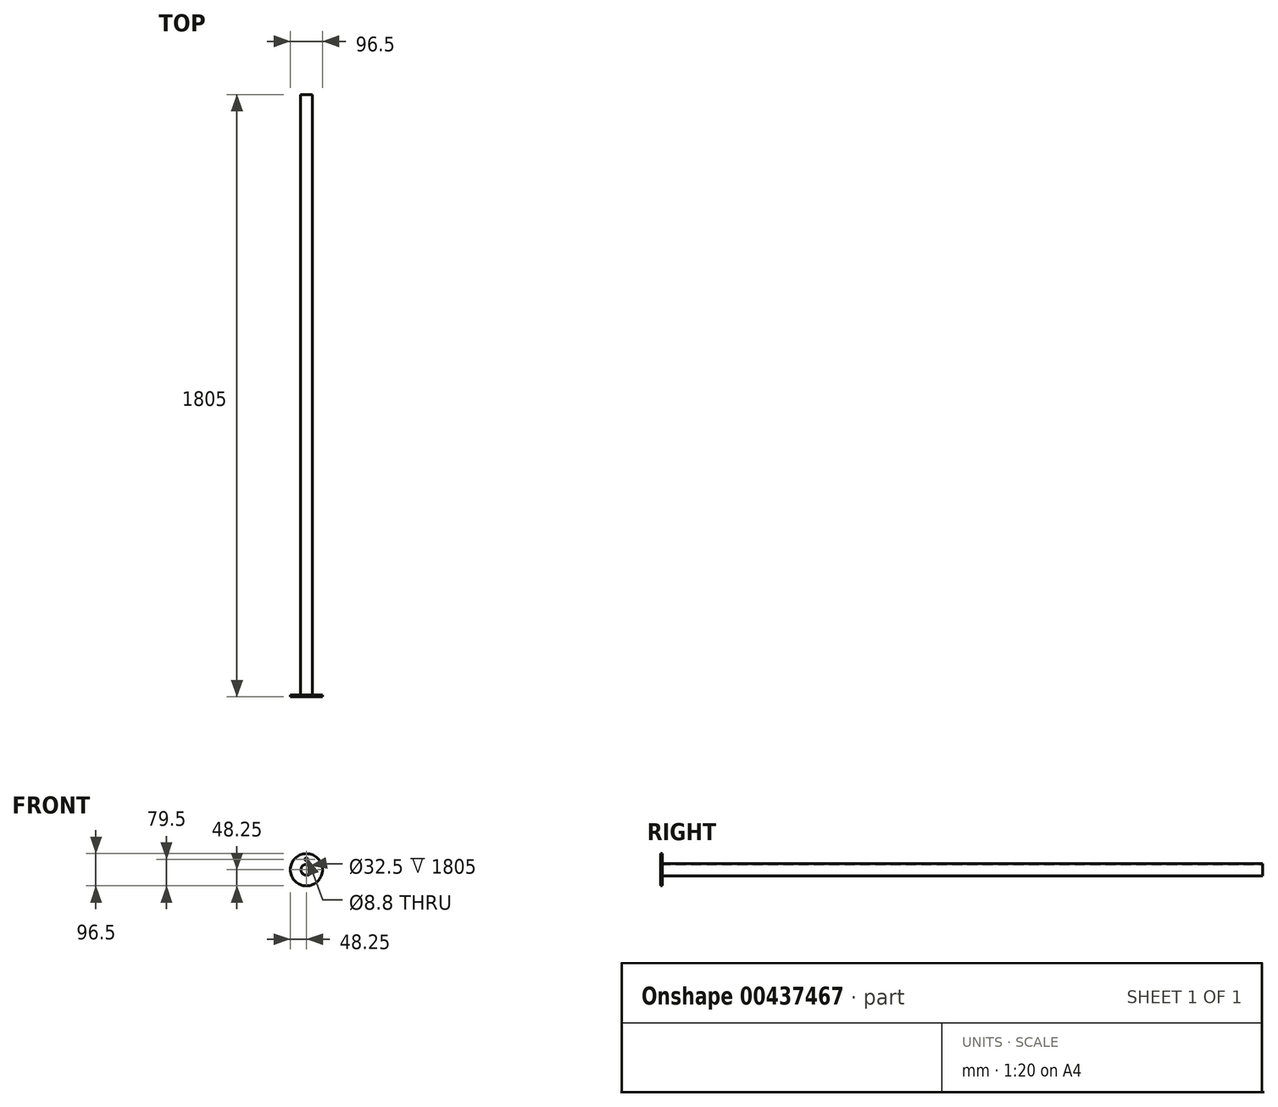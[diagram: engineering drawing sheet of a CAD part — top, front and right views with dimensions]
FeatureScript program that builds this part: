
annotation { "Feature Type Name" : "Feature", "Feature Type Description" : "" }
export const myFeature = defineFeature(function(context is Context, id is Id, definition is map)
    precondition{}
    {
        {
            var Q0;
            Q0=qCreatedBy(makeId("Front.planeOp"),FACE);
            var sketch = newSketch(context, id + "F0", { "sketchPlane" : qUnion([Q0])});
            skCircle(sketch, "E0", {"center": v(0, 0) * mm, "radius": 18.25 * mm});
            skCircle(sketch, "E1", {"center": v(0, 0) * mm, "radius": 16.25 * mm});
            skSolve(sketch);
        }
        {
            var Q0;
            Q0=makeQuery(id+"F0.imprint","IMPRINT",FACE,{"disambiguationData":[TD([[makeQuery(id+"F0.imprint","IMPRINT",EDGE,{"derivedFrom":sQuery(id+"F0.wireOp",EDGE,"E0")}),1.0]])]});
            extrude(context, id + "F1", {"entities" : qUnion([Q0]), "depth" : 1800 * mm});
        }
        {
            var Q0;
            Q0=makeQuery(id+"F1.opExtrude","CAP_FACE",FACE,{"disambiguationData":[OSD([sQuery(id+"F0.wireOp",EDGE,"E0"),sQuery(id+"F0.wireOp",EDGE,"E1")])],"isStart":false});
            var sketch = newSketch(context, id + "F2", { "sketchPlane" : qUnion([Q0])});
            skCircle(sketch, "E2", {"center": v(0, 0) * mm, "radius": 48.25 * mm});
            skSolve(sketch);
        }
        {
            var Q0;
            Q0=makeQuery(id+"F2.imprint","IMPRINT",FACE,{"disambiguationData":[TD([[makeQuery(id+"F2.imprint","IMPRINT",EDGE,{"derivedFrom":sQuery(id+"F2.wireOp",EDGE,"E2")}),1.0]])]});
            var Q1;
            Q1=makeQuery(id+"F2.imprint","IMPRINT",FACE,{"disambiguationData":[TD([[makeQuery(id+"F2.imprint","IMPRINT",EDGE,{"derivedFrom":makeQuery(id+"F1.opExtrude","CAP_EDGE",EDGE,{"disambiguationData":[OSD([sQuery(id+"F0.wireOp",EDGE,"E0")])],"isStart":false})}),1.0]])]});
            extrude(context, id + "F3", {"entities" : qUnion([Q0, Q1]), "operationType" : NewBodyOperationType.ADD, "depth" : 5 * mm});
        }
        {
            var Q0;
            Q0=makeQuery(id+"F3.opExtrude","CAP_FACE",FACE,{"disambiguationData":[OSD([sQuery(id+"F0.wireOp",EDGE,"E1"),sQuery(id+"F2.wireOp",EDGE,"E2")])],"isStart":false});
            var sketch = newSketch(context, id + "F4", { "sketchPlane" : qUnion([Q0])});
            skPoint(sketch, "E3", {"position": v(0, 31.25) * mm});
            skSolve(sketch);
        }
        {
            var Q0;
            Q0=sQuery(id+"F4.wireOp",VERTEX,"E3");
            var Q1;
            Q1=makeQuery(id+"F1.opExtrude","SWEPT_BODY",BODY,{"disambiguationData":[OSD([sQuery(id+"F0.wireOp",EDGE,"E0"),sQuery(id+"F0.wireOp",EDGE,"E1")])]});
            hole(context, id + "F5", {"style" : HoleStyle.SIMPLE, "endStyle" : HoleEndStyle.THROUGH, "standardTappedOrClearance" : lookupTablePath({ "standard" : "ISO", "engagement" : "75%", "pitch" : "1.25 mm", "size" : "M10", "type" : "Tapped" }), "standardBlindInLast" : lookupTablePath({ "standard" : "ISO", "engagement" : "75%", "pitch" : "1.25 mm", "size" : "M10", "type" : "Tapped" }), "holeDiameter" : 8.8 * mm, "showTappedDepth" : true, "isTappedThrough" : true, "tappedDepth" : 6.25 * mm, "tapClearance" : 3, "locations" : qUnion([Q0]), "scope" : qUnion([Q1]), "majorDiameter" : 10 * mm});
        }
    });
